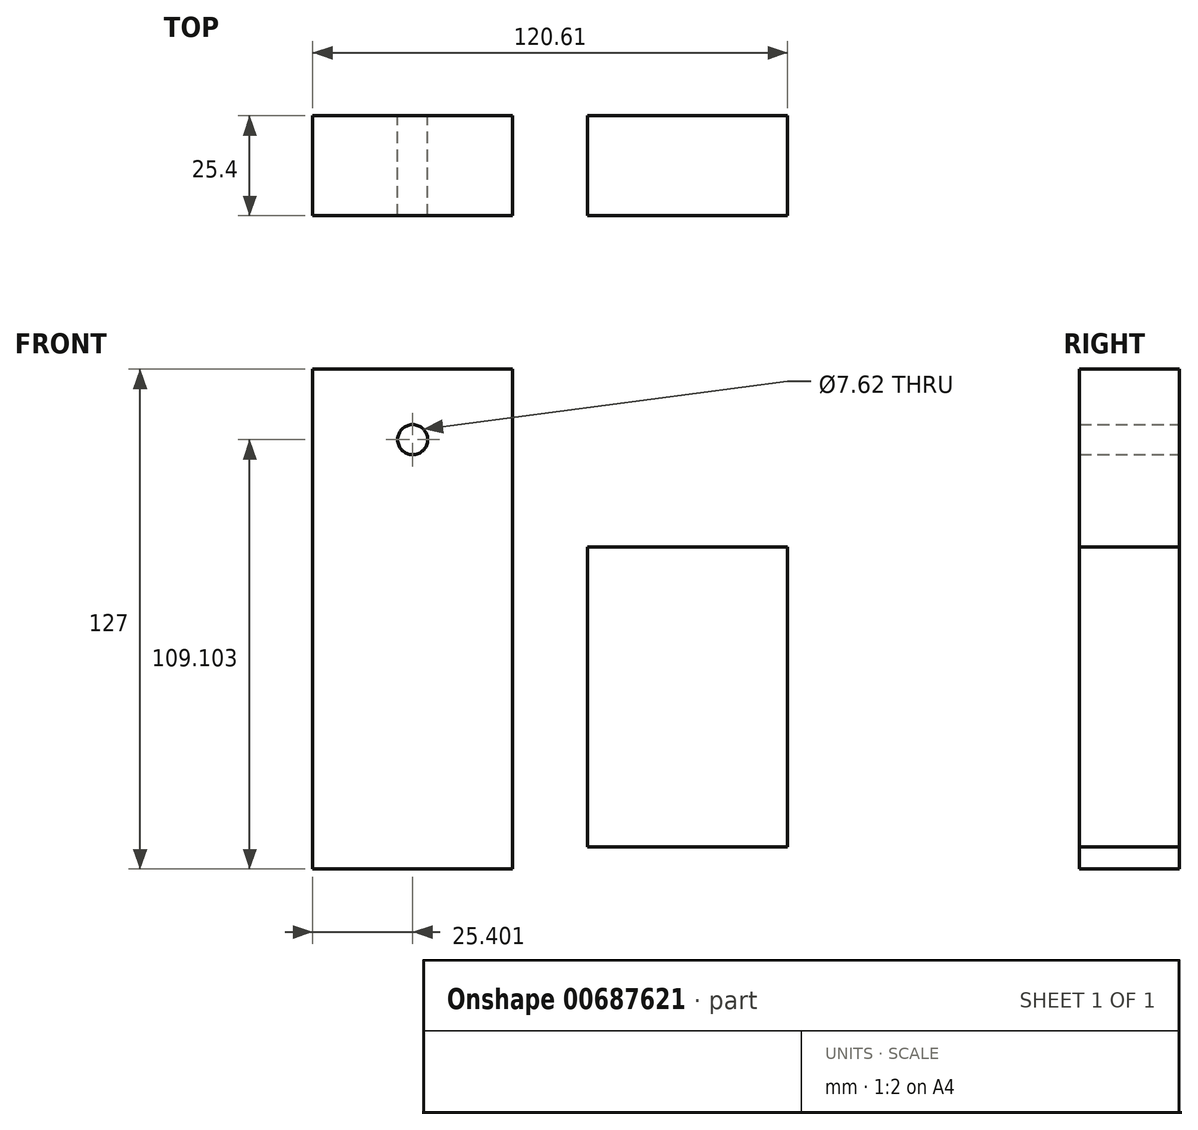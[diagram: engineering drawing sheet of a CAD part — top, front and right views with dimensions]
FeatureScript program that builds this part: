
annotation { "Feature Type Name" : "Feature", "Feature Type Description" : "" }
export const myFeature = defineFeature(function(context is Context, id is Id, definition is map)
    precondition{}
    {
        {
            var Q0;
            Q0=qCreatedBy(makeId("Front.planeOp"),FACE);
            var sketch = newSketch(context, id + "F0", { "sketchPlane" : qUnion([Q0])});
            skLineSegment(sketch, "E0.bottom", {"start": v(-62.8, 45.2) * mm, "end": v(-12, 45.2) * mm});
            skLineSegment(sketch, "E0.top", {"start": v(-62.8, -81.8) * mm, "end": v(-12, -81.8) * mm});
            skLineSegment(sketch, "E0.left", {"start": v(-62.8, 45.2) * mm, "end": v(-62.8, -81.8) * mm});
            skLineSegment(sketch, "E0.right", {"start": v(-12, 45.2) * mm, "end": v(-12, -81.8) * mm});
            skLineSegment(sketch, "E1.bottom", {"start": v(7.01, 0) * mm, "end": v(57.81, 0) * mm});
            skLineSegment(sketch, "E1.top", {"start": v(7.01, -76.2) * mm, "end": v(57.81, -76.2) * mm});
            skLineSegment(sketch, "E1.left", {"start": v(7.01, 0) * mm, "end": v(7.01, -76.2) * mm});
            skLineSegment(sketch, "E1.right", {"start": v(57.81, 0) * mm, "end": v(57.81, -76.2) * mm});
            skCircle(sketch, "E2", {"center": v(-37.4, 27.3) * mm, "radius": 3.81 * mm});
            skPoint(sketch, "E2.centerSnap0", {"position": v(-37.4, 45.2) * mm});
            skSolve(sketch);
        }
        {
            var Q0;
            Q0=makeQuery(id+"F0.imprint","IMPRINT",FACE,{"disambiguationData":[TD([[makeQuery(id+"F0.imprint","IMPRINT",EDGE,{"derivedFrom":sQuery(id+"F0.wireOp",EDGE,"E0.bottom")}),-1.0]])]});
            var Q1;
            Q1=makeQuery(id+"F0.imprint","IMPRINT",FACE,{"disambiguationData":[TD([[makeQuery(id+"F0.imprint","IMPRINT",EDGE,{"derivedFrom":sQuery(id+"F0.wireOp",EDGE,"E1.bottom")}),-1.0]])]});
            extrude(context, id + "F1", {"entities" : qUnion([Q0, Q1]), "depth" : 25.4 * mm, "offsetDistance" : 25.4 * mm});
        }
    });
